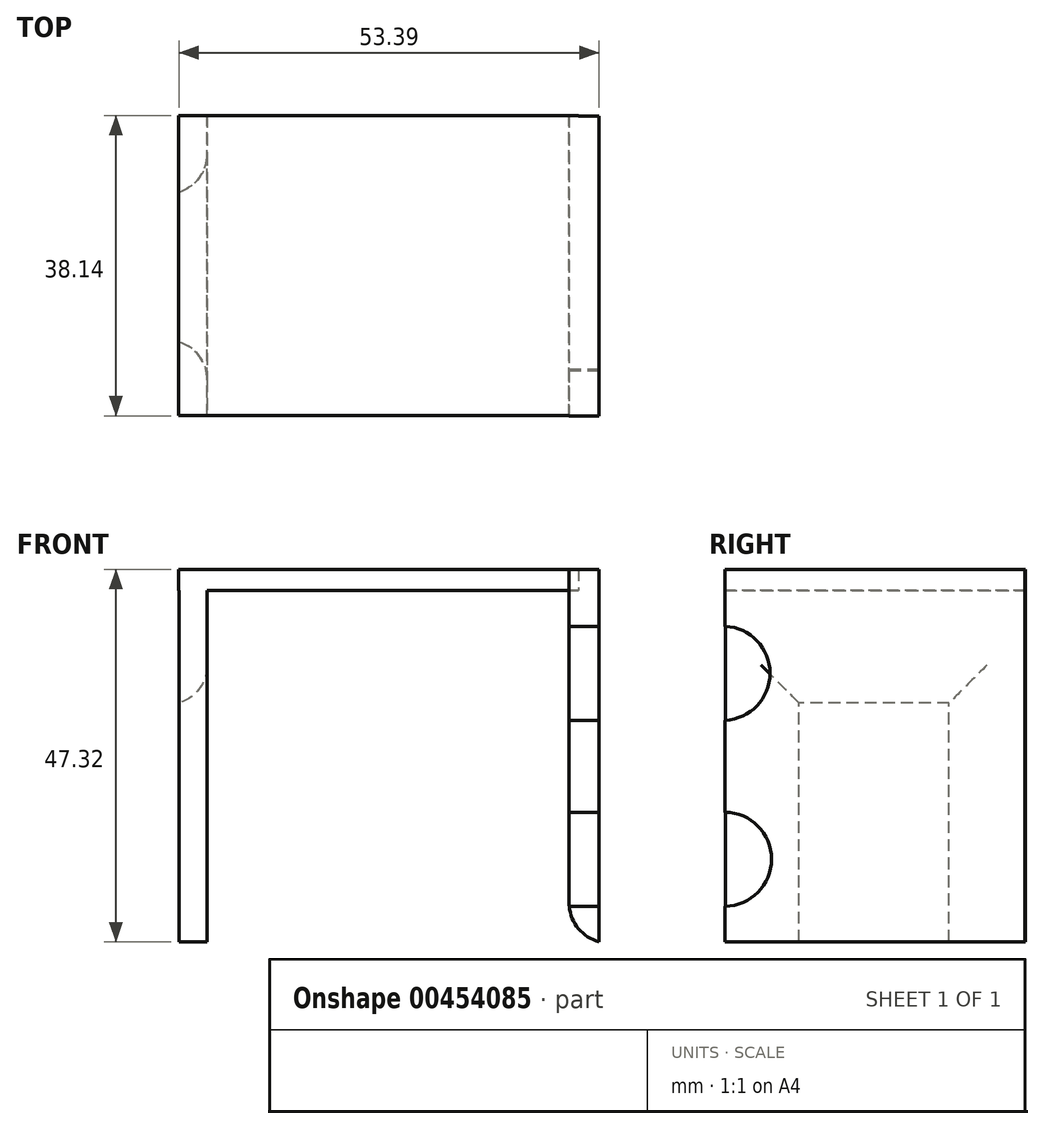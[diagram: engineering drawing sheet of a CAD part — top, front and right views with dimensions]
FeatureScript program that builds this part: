
annotation { "Feature Type Name" : "Feature", "Feature Type Description" : "" }
export const myFeature = defineFeature(function(context is Context, id is Id, definition is map)
    precondition{}
    {
        {
            var Q0;
            Q0=qCreatedBy(makeId("Top.planeOp"),FACE);
            var sketch = newSketch(context, id + "F0", { "sketchPlane" : qUnion([Q0])});
            skLineSegment(sketch, "E0.bottom", {"start": v(-21.9, 25.72) * mm, "end": v(28.9, 25.72) * mm});
            skLineSegment(sketch, "E0.top", {"start": v(-21.9, -12.38) * mm, "end": v(28.9, -12.38) * mm});
            skLineSegment(sketch, "E0.left", {"start": v(-21.9, 25.72) * mm, "end": v(-21.9, -12.38) * mm});
            skLineSegment(sketch, "E0.right", {"start": v(28.9, 25.72) * mm, "end": v(28.9, -12.38) * mm});
            skSolve(sketch);
        }
        {
            var Q0;
            Q0=qSketchRegion(id+"F0",true);
            extrude(context, id + "F1", {"entities" : qUnion([Q0]), "depth" : 3.17 * mm});
        }
        {
            var Q0;
            Q0=qCreatedBy(makeId("Right.planeOp"),FACE);
            var sketch = newSketch(context, id + "F2", { "sketchPlane" : qUnion([Q0])});
            skLineSegment(sketch, "E1.bottom", {"start": v(25.71, 2.97) * mm, "end": v(-12.39, 2.97) * mm});
            skLineSegment(sketch, "E1.top", {"start": v(25.71, -44.65) * mm, "end": v(-12.39, -44.65) * mm});
            skLineSegment(sketch, "E1.left", {"start": v(25.71, 2.97) * mm, "end": v(25.71, -44.65) * mm});
            skLineSegment(sketch, "E1.right", {"start": v(-12.39, 2.97) * mm, "end": v(-12.39, -44.65) * mm});
            skSolve(sketch);
        }
        {
            var Q0;
            Q0=qSketchRegion(id+"F2",true);
            extrude(context, id + "F3", {"entities" : qUnion([Q0]), "operationType" : NewBodyOperationType.ADD, "oppositeDirection" : true, "depth" : 21.84 * mm, "hasSecondDirection" : true, "secondDirectionOppositeDirection" : true, "secondDirectionDepth" : 18.29 * mm});
        }
        {
            var Q0;
            Q0=qCreatedBy(makeId("Right.planeOp"),FACE);
            var sketch = newSketch(context, id + "F4", { "sketchPlane" : qUnion([Q0])});
            skLineSegment(sketch, "E2.bottom", {"start": v(25.68, 3) * mm, "end": v(-12.42, 3) * mm});
            skLineSegment(sketch, "E2.top", {"start": v(25.68, -44.62) * mm, "end": v(-12.42, -44.62) * mm});
            skLineSegment(sketch, "E2.left", {"start": v(25.68, 3) * mm, "end": v(25.68, -44.62) * mm});
            skLineSegment(sketch, "E2.right", {"start": v(-12.42, 3) * mm, "end": v(-12.42, -44.62) * mm});
            skSolve(sketch);
        }
        {
            var Q0;
            Q0=qSketchRegion(id+"F4",true);
            extrude(context, id + "F5", {"entities" : qUnion([Q0]), "operationType" : NewBodyOperationType.ADD, "depth" : 31.5 * mm, "hasSecondDirection" : true, "secondDirectionOppositeDirection" : false, "secondDirectionDepth" : 27.7 * mm});
        }
        {
            var Q0;
            Q0=qCreatedBy(makeId("Right.planeOp"),FACE);
            var sketch = newSketch(context, id + "F6", { "sketchPlane" : qUnion([Q0])});
            skLineSegment(sketch, "E3.bottom", {"start": v(16.02, -68.28) * mm, "end": v(-3.03, -68.28) * mm});
            skLineSegment(sketch, "E3.top", {"start": v(16.02, -14.3) * mm, "end": v(-3.03, -14.3) * mm});
            skLineSegment(sketch, "E3.left", {"start": v(16.02, -68.28) * mm, "end": v(16.02, -14.3) * mm});
            skLineSegment(sketch, "E3.right", {"start": v(-3.03, -68.28) * mm, "end": v(-3.03, -14.3) * mm});
            skSolve(sketch);
        }
        {
            var Q0;
            Q0=qSketchRegion(id+"F6",true);
            extrude(context, id + "F7", {"entities" : qUnion([Q0]), "operationType" : NewBodyOperationType.REMOVE, "oppositeDirection" : true, "depth" : 32 * mm});
        }
        {
            var Q0;
            Q0=makeQuery(id+"F7.boolean.opBoolean","INTERSECT",EDGE,{"derivedFrom":[makeQuery(id+"F3.opExtrude","CAP_FACE",FACE,{"disambiguationData":[OSD([sQuery(id+"F2.wireOp",EDGE,"E1.bottom"),sQuery(id+"F2.wireOp",EDGE,"E1.top"),sQuery(id+"F2.wireOp",EDGE,"E1.left"),sQuery(id+"F2.wireOp",EDGE,"E1.right")])],"isStart":true}),makeQuery(id+"F7.opExtrude","SWEPT_FACE",FACE,{"disambiguationData":[OSD([sQuery(id+"F6.wireOp",EDGE,"E3.left")])]})]});
            var Q1;
            Q1=makeQuery(id+"F7.boolean.opBoolean","INTERSECT",EDGE,{"derivedFrom":[makeQuery(id+"F3.opExtrude","CAP_FACE",FACE,{"disambiguationData":[OSD([sQuery(id+"F2.wireOp",EDGE,"E1.bottom"),sQuery(id+"F2.wireOp",EDGE,"E1.top"),sQuery(id+"F2.wireOp",EDGE,"E1.left"),sQuery(id+"F2.wireOp",EDGE,"E1.right")])],"isStart":true}),makeQuery(id+"F7.opExtrude","SWEPT_FACE",FACE,{"disambiguationData":[OSD([sQuery(id+"F6.wireOp",EDGE,"E3.top")])]})]});
            var Q2;
            Q2=makeQuery(id+"F7.boolean.opBoolean","INTERSECT",EDGE,{"derivedFrom":[makeQuery(id+"F3.opExtrude","CAP_FACE",FACE,{"disambiguationData":[OSD([sQuery(id+"F2.wireOp",EDGE,"E1.bottom"),sQuery(id+"F2.wireOp",EDGE,"E1.top"),sQuery(id+"F2.wireOp",EDGE,"E1.left"),sQuery(id+"F2.wireOp",EDGE,"E1.right")])],"isStart":true}),makeQuery(id+"F7.opExtrude","SWEPT_FACE",FACE,{"disambiguationData":[OSD([sQuery(id+"F6.wireOp",EDGE,"E3.right")])]})]});
            var Q3;
            Q3=makeQuery(id+"F5.opExtrude","CAP_EDGE",EDGE,{"disambiguationData":[OSD([sQuery(id+"F4.wireOp",EDGE,"E2.top")])],"isStart":true});
            fillet(context, id + "F8", {"entities" : qUnion([Q0, Q1, Q2, Q3]), "radius" : 5.08 * mm, "tangentPropagation" : true, "allowEdgeOverflow" : false});
        }
        {
            var Q0;
            Q0=qCreatedBy(makeId("Front.planeOp"),FACE);
            var sketch = newSketch(context, id + "F9", { "sketchPlane" : qUnion([Q0])});
            skLineSegment(sketch, "E4.bottom", {"start": v(-22.82, 4.16) * mm, "end": v(32.1, 4.16) * mm});
            skLineSegment(sketch, "E4.top", {"start": v(-22.82, 2.67) * mm, "end": v(32.1, 2.67) * mm});
            skLineSegment(sketch, "E4.left", {"start": v(-22.82, 4.16) * mm, "end": v(-22.82, 2.67) * mm});
            skLineSegment(sketch, "E4.right", {"start": v(32.1, 4.16) * mm, "end": v(32.1, 2.67) * mm});
            skSolve(sketch);
        }
        {
            var Q0;
            Q0=qSketchRegion(id+"F9",true);
            extrude(context, id + "F10", {"entities" : qUnion([Q0]), "operationType" : NewBodyOperationType.REMOVE, "oppositeDirection" : true, "depth" : 28.5 * mm, "hasSecondDirection" : true, "secondDirectionOppositeDirection" : false, "secondDirectionDepth" : 25.4 * mm});
        }
        {
            var Q0;
            Q0=qCreatedBy(makeId("Right.planeOp"),FACE);
            var sketch = newSketch(context, id + "F11", { "sketchPlane" : qUnion([Q0])});
            skCircle(sketch, "E5", {"center": v(-12.49, -34.15) * mm, "radius": 5.97 * mm});
            skCircle(sketch, "E6", {"center": v(-12.68, -10.53) * mm, "radius": 5.97 * mm});
            skSolve(sketch);
        }
        {
            var Q0;
            Q0 = qSketchRegion(id + "F11", true);
            extrude(context, id + "F12", {"entities" : qUnion([Q0]), "operationType" : NewBodyOperationType.REMOVE, "depth" : 52.07 * mm});
        }
    });
